# Revit family: axor_basic_set_for_flexaplus_finish_set_58314180_
name_source: partatom
category: Plumbing Fixtures
revit_build: Autodesk Revit 2015 (Build: 20140903_1530(x64)
units: mm (PartAtom-declared; Revit-internal decimal feet)

## types (1)
- n.a.
    BIMobject category = Drainage
    BOSUseNativeGeometries = 1
    Default Elevation = 1219 mm
    Design country = Germany
    EAN code = https://4059625077665
    Edition number = 1
    IFC Classification = Sanitary Terminal
    Installation instructions = https://pro.hansgrohe-int.com
    Manufacturer country = Germany
    Manufacturer name = AXOR
    Masterformat 2014 Code = 33 37 00
    Masterformat 2014 Description = Overflow Control
    NBS Reference Code = 95-50-xx
    NBS Reference Description = Overflows
    Nominal height = 0
    Nominal width = 0
    OmniClass Code = 23-27 29 25 11
    OmniClass Description = Overflow Regulators
    Product Guid = 3cc175fc-28cd-4aa5-871e-7ce942f4b9a2
    Product SKU = 58314180
    Product data url = https://bimobject.com
    Product family = Wastes and overflows
    Product group = Bath filler with wastes and overflow for bath tubs
    Product name = AXOR Basic set for Flexaplus finish set 58314180
    Product url = https://pro.hansgrohe-int.com
    QR code = http://bimobject.com
    Technical description = https://pro.hansgrohe-int.com
    UNSPSC Code = 4710
    Uniclass 1.4 Code = L21712
    Uniclass 1.4 Description = Water distribution systems products
    Uniclass 2.0 Code = PR-35-06-07
    Uniclass 2.0 Description = Bath Water Supply Fittings
    Uniclass 2015 Code = Pr_60_45_90
    Uniclass 2015 Name = Wastewater and water mixer products
    Uniformat II Code = D2020
    Uniformat II Description = Domestic Water Distribution
    Weight Net (Kg) = 0

## geometry (parser evidence)
native form markers: Sweep x1
no freeform markers — native parametric forms only
